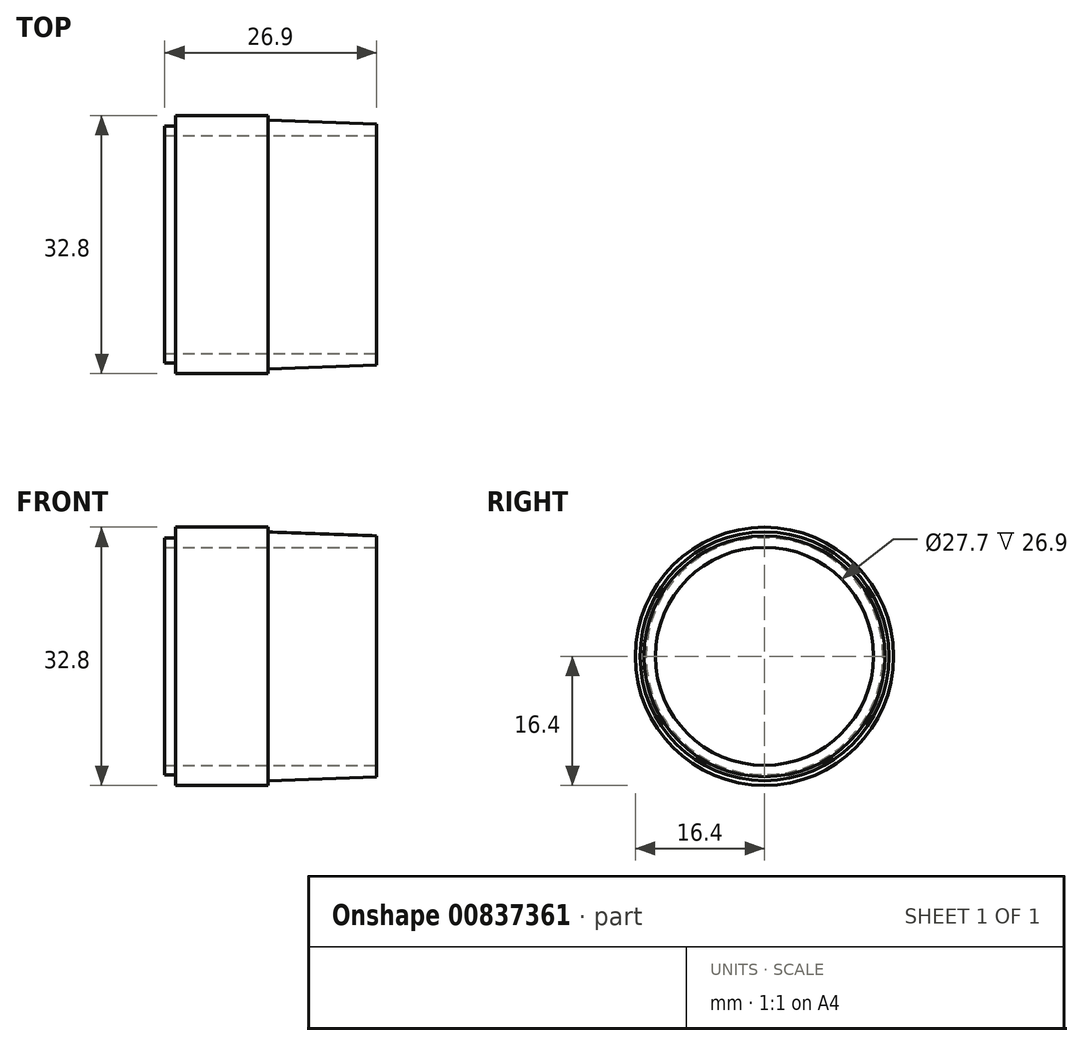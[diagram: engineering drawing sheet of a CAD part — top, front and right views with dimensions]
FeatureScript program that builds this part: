
annotation { "Feature Type Name" : "Feature", "Feature Type Description" : "" }
export const myFeature = defineFeature(function(context is Context, id is Id, definition is map)
    precondition{}
    {
        {
            var Q0;
            Q0=qCreatedBy(makeId("Front.planeOp"),FACE);
            var sketch = newSketch(context, id + "F0", { "sketchPlane" : qUnion([Q0])});
            skLineSegment(sketch, "E0.bottom", {"start": v(-26.9, 16.4) * mm, "end": v(-13.8, 16.4) * mm});
            skLineSegment(sketch, "E0.top", {"start": v(-26.9, 0) * mm, "end": v(-13.8, 0) * mm});
            skLineSegment(sketch, "E0.left", {"start": v(-26.9, 16.4) * mm, "end": v(-26.9, 0) * mm});
            skLineSegment(sketch, "E0.right", {"start": v(-13.8, 16.4) * mm, "end": v(-13.8, 0) * mm});
            skLineSegment(sketch, "E1", {"start": v(-13.8, 15.8) * mm, "end": v(-13.8, 0) * mm});
            skLineSegment(sketch, "E2", {"start": v(-13.8, 0) * mm, "end": v(0, 0) * mm});
            skLineSegment(sketch, "E3", {"start": v(0, 0) * mm, "end": v(0, 15.3) * mm});
            skLineSegment(sketch, "E4", {"start": v(0, 15.3) * mm, "end": v(-13.8, 15.8) * mm});
            skSolve(sketch);
        }
        {
            var Q0;
            Q0 = qSketchRegion(id + "F0", true);
            var Q1;
            Q1=sQuery(id+"F0.wireOp",EDGE,"E0.top");
            revolve(context, id + "F1", {"surfaceOperationType" : NewSurfaceOperationType.NEW, "entities" : qUnion([Q0]), "axis" : qUnion([Q1]), "revolveType" : RevolveType.FULL});
        }
        {
            var Q0;
            Q0=makeQuery(id+"F1.opRevolve","SWEPT_FACE",FACE,{"disambiguationData":[OSD([sQuery(id+"F0.wireOp",EDGE,"E3")])]});
            var sketch = newSketch(context, id + "F2", { "sketchPlane" : qUnion([Q0])});
            skCircle(sketch, "E5", {"center": v(0, 0) * mm, "radius": 13.85 * mm});
            skSolve(sketch);
        }
        {
            var Q0;
            Q0 = qSketchRegion(id + "F2", true);
            extrude(context, id + "F3", {"entities" : qUnion([Q0]), "operationType" : NewBodyOperationType.REMOVE, "endBound" : BoundingType.THROUGH_ALL, "oppositeDirection" : true, "depth" : 25 * mm, "offsetDistance" : 25 * mm});
        }
        {
            var Q0;
            Q0=makeQuery(id+"F1.opRevolve","SWEPT_FACE",FACE,{"disambiguationData":[OSD([sQuery(id+"F0.wireOp",EDGE,"E0.left")])]});
            var sketch = newSketch(context, id + "F4", { "sketchPlane" : qUnion([Q0])});
            skCircle(sketch, "E6", {"center": v(0, 0) * mm, "radius": 15.05 * mm});
            skSolve(sketch);
        }
        {
            var Q0;
            Q0=makeQuery(id+"F4.imprint","IMPRINT",FACE,{"disambiguationData":[TD([[makeQuery(id+"F4.imprint","IMPRINT",EDGE,{"derivedFrom":sQuery(id+"F4.wireOp",EDGE,"E6")}),-1.0]])]});
            extrude(context, id + "F5", {"entities" : qUnion([Q0]), "operationType" : NewBodyOperationType.REMOVE, "oppositeDirection" : true, "depth" : 1.4 * mm, "offsetDistance" : 25 * mm});
        }
    });
